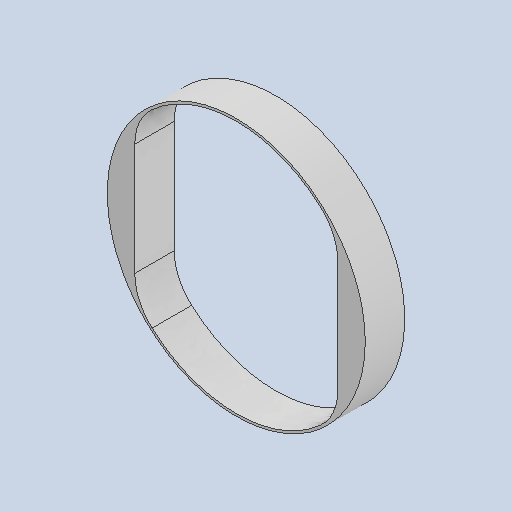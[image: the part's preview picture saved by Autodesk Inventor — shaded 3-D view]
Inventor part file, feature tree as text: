
AUTODESK INVENTOR PART (.ipt)
format: ipt  version: 2022 (Build 260153000, 153)  size: 113,664 bytes
history: native  units: in
note: dims shown in document units (in); Inventor stores cm internally (conversion verified against a paired STEP export)
features: other x3, sketch x1, plane x1
ambient origin geometry x8: Origin, YZ Plane, XZ Plane, XY Plane, X Axis, Y Axis, Z Axis, Center Point
bodies: Solid1 (feature_tree)
feature tree (5):
  other  "encoderring.ipt"
  other  "Solid1::encoderring.ipt"
  other  "TaggingFeature1"
  sketch  "Sketch1"  dims[d0=0.3937in]
  plane  "Work Plane1"
